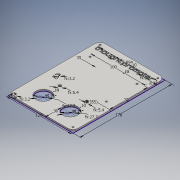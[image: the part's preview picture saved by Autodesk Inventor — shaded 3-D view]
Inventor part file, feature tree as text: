
AUTODESK INVENTOR PART (.ipt)
format: ipt  version: 2016 (Build 200138000, 138)  size: 573,952 bytes
history: native  units: mm
features: extrude x2, sketch x1, fillet x1
ambient origin geometry x8: Origin, YZ Plane, XZ Plane, XY Plane, X Axis, Y Axis, Z Axis, Center Point
bodies: Solid1 (feature_tree)
feature tree (4):
  sketch  "Sketch1"  dims[d0=120.0mm d1=170.0mm d2=27.7mm d4=5.4mm d5=5.4mm d10=35.0mm d11=30.0mm d12=35.75mm d13=10.0mm d14=35.0mm d15=27.7mm d16=35.75mm d17=10.0mm d18=3.2mm d19=5.0mm d21=5.0mm d22=10.0mm d23=10.0mm d24=100.0mm d25=70.0mm d26=8.369892mm d27=8.355108mm d28=3.2mm d29=5.0mm d30=5.0mm d31=105.894247mm d32=3.0mm d33=0.0mm d34=10.0mm d35=4.0mm d36=0.0mm]
  extrude  "Extrusion1"  Depth=170.0mm
  fillet  "Fillet1"  Radius=27.7mm
  extrude  "Extrusion2"  Depth=5.4mm
